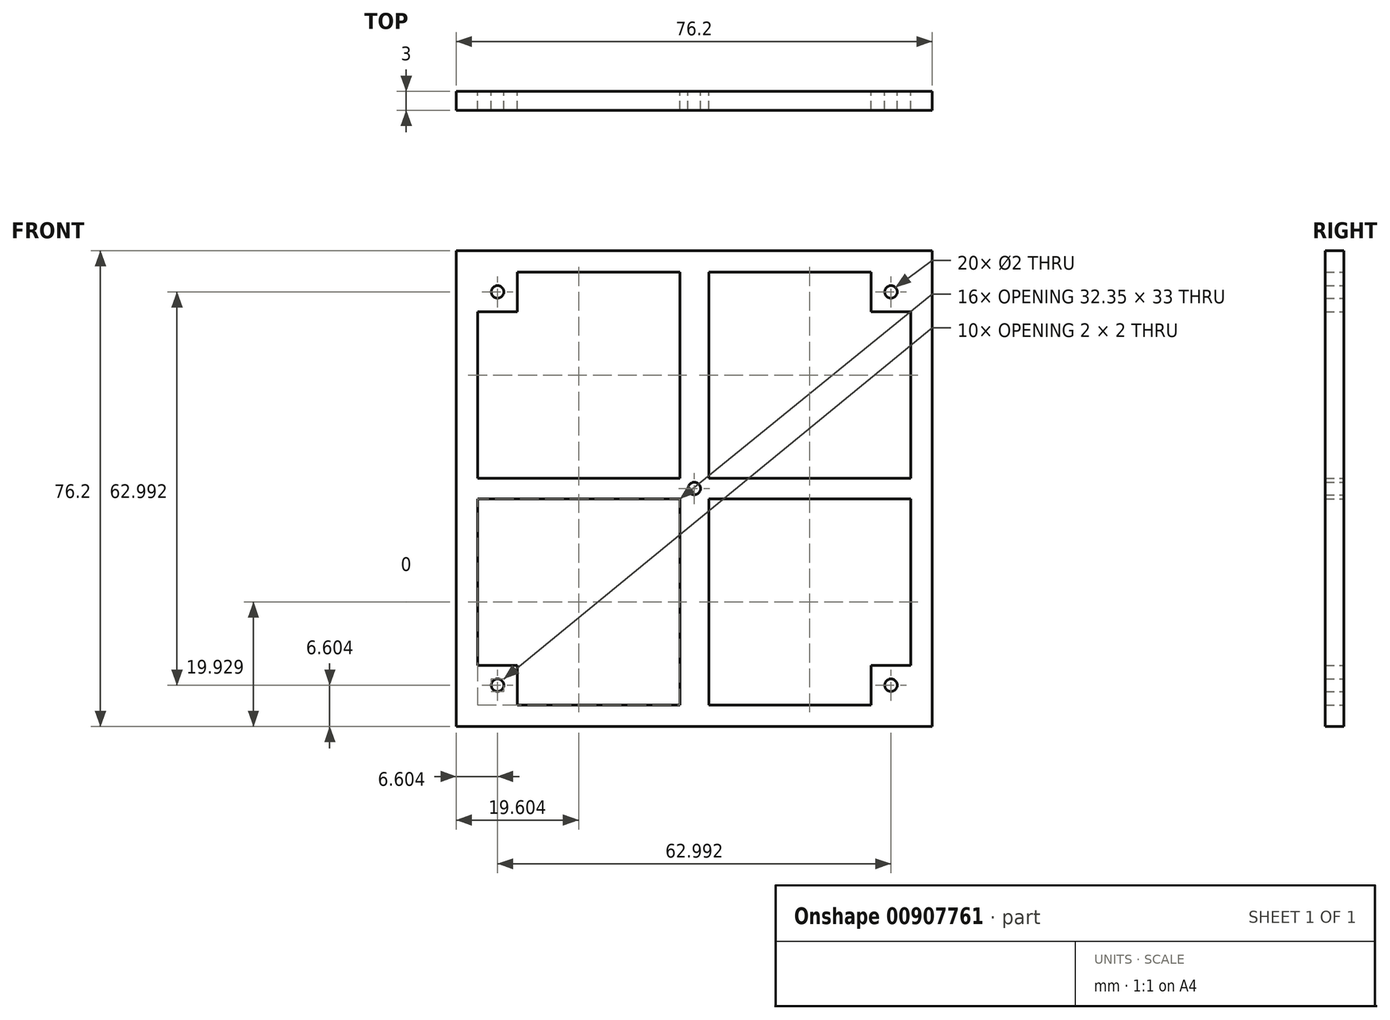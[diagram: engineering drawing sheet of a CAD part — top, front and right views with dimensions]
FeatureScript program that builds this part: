
annotation { "Feature Type Name" : "Feature", "Feature Type Description" : "" }
export const myFeature = defineFeature(function(context is Context, id is Id, definition is map)
    precondition{}
    {
        {
            var Q0;
            Q0=qCreatedBy(makeId("Front.planeOp"),FACE);
            var sketch = newSketch(context, id + "F0", { "sketchPlane" : qUnion([Q0])});
            skLineSegment(sketch, "E0.bottom", {"start": v(38.1, 38.1) * mm, "end": v(-38.1, 38.1) * mm});
            skLineSegment(sketch, "E0.top", {"start": v(38.1, -38.1) * mm, "end": v(-38.1, -38.1) * mm});
            skLineSegment(sketch, "E0.left", {"start": v(38.1, 38.1) * mm, "end": v(38.1, -38.1) * mm});
            skLineSegment(sketch, "E0.right", {"start": v(-38.1, 38.1) * mm, "end": v(-38.1, -38.1) * mm});
            skPoint(sketch, "E0.middle", {"position": v(0, 0) * mm});
            skPoint(sketch, "E1", {"position": v(-31.5, 31.5) * mm});
            skPoint(sketch, "E2", {"position": v(31.5, 31.5) * mm});
            skPoint(sketch, "E3", {"position": v(31.5, -31.5) * mm});
            skPoint(sketch, "E4", {"position": v(-31.5, -31.5) * mm});
            skLineSegment(sketch, "E5.bottom", {"start": v(-28.32, 34.67) * mm, "end": v(-34.67, 34.67) * mm});
            skLineSegment(sketch, "E5.top", {"start": v(-28.32, 28.32) * mm, "end": v(-34.67, 28.32) * mm});
            skLineSegment(sketch, "E5.left", {"start": v(-28.32, 34.67) * mm, "end": v(-28.32, 28.32) * mm});
            skLineSegment(sketch, "E5.right", {"start": v(-34.67, 34.67) * mm, "end": v(-34.67, 28.32) * mm});
            skLineSegment(sketch, "E6.bottom", {"start": v(34.67, 34.67) * mm, "end": v(28.32, 34.67) * mm});
            skLineSegment(sketch, "E6.top", {"start": v(34.67, 28.32) * mm, "end": v(28.32, 28.32) * mm});
            skLineSegment(sketch, "E6.left", {"start": v(34.67, 34.67) * mm, "end": v(34.67, 28.32) * mm});
            skLineSegment(sketch, "E6.right", {"start": v(28.32, 34.67) * mm, "end": v(28.32, 28.32) * mm});
            skLineSegment(sketch, "E7.bottom", {"start": v(34.67, -28.32) * mm, "end": v(28.32, -28.32) * mm});
            skLineSegment(sketch, "E7.top", {"start": v(34.67, -34.67) * mm, "end": v(28.32, -34.67) * mm});
            skLineSegment(sketch, "E7.left", {"start": v(34.67, -28.32) * mm, "end": v(34.67, -34.67) * mm});
            skLineSegment(sketch, "E7.right", {"start": v(28.32, -28.32) * mm, "end": v(28.32, -34.67) * mm});
            skLineSegment(sketch, "E8.bottom", {"start": v(-28.32, -28.32) * mm, "end": v(-34.67, -28.32) * mm});
            skLineSegment(sketch, "E8.top", {"start": v(-28.32, -34.67) * mm, "end": v(-34.67, -34.67) * mm});
            skLineSegment(sketch, "E8.left", {"start": v(-28.32, -28.32) * mm, "end": v(-28.32, -34.67) * mm});
            skLineSegment(sketch, "E8.right", {"start": v(-34.67, -28.32) * mm, "end": v(-34.67, -34.67) * mm});
            skLineSegment(sketch, "E9.bottom", {"start": v(-28.32, 34.67) * mm, "end": v(-2.32, 34.67) * mm});
            skLineSegment(sketch, "E9.top", {"start": v(-28.32, 1.67) * mm, "end": v(-2.32, 1.67) * mm});
            skLineSegment(sketch, "E9.left", {"start": v(-28.32, 34.67) * mm, "end": v(-28.32, 1.67) * mm});
            skLineSegment(sketch, "E9.right", {"start": v(-2.32, 34.67) * mm, "end": v(-2.32, 1.67) * mm});
            skLineSegment(sketch, "E10.bottom", {"start": v(28.32, 34.67) * mm, "end": v(2.32, 34.67) * mm});
            skLineSegment(sketch, "E10.top", {"start": v(28.32, 1.67) * mm, "end": v(2.32, 1.67) * mm});
            skLineSegment(sketch, "E10.left", {"start": v(28.32, 34.67) * mm, "end": v(28.32, 1.67) * mm});
            skLineSegment(sketch, "E10.right", {"start": v(2.32, 34.67) * mm, "end": v(2.32, 1.67) * mm});
            skLineSegment(sketch, "E11.bottom", {"start": v(-28.32, -34.67) * mm, "end": v(-2.32, -34.67) * mm});
            skLineSegment(sketch, "E11.top", {"start": v(-28.32, -1.67) * mm, "end": v(-2.32, -1.67) * mm});
            skLineSegment(sketch, "E11.left", {"start": v(-28.32, -34.67) * mm, "end": v(-28.32, -1.67) * mm});
            skLineSegment(sketch, "E11.right", {"start": v(-2.32, -34.67) * mm, "end": v(-2.32, -1.67) * mm});
            skLineSegment(sketch, "E12.bottom", {"start": v(28.32, -34.67) * mm, "end": v(2.32, -34.67) * mm});
            skLineSegment(sketch, "E12.top", {"start": v(28.32, -1.67) * mm, "end": v(2.32, -1.67) * mm});
            skLineSegment(sketch, "E12.left", {"start": v(28.32, -34.67) * mm, "end": v(28.32, -1.67) * mm});
            skLineSegment(sketch, "E12.right", {"start": v(2.32, -34.67) * mm, "end": v(2.32, -1.67) * mm});
            skLineSegment(sketch, "E13.top", {"start": v(34.67, 1.67) * mm, "end": v(28.32, 1.67) * mm});
            skLineSegment(sketch, "E13.left", {"start": v(34.67, 28.32) * mm, "end": v(34.67, 1.67) * mm});
            skLineSegment(sketch, "E13.right", {"start": v(28.32, 28.32) * mm, "end": v(28.32, 1.67) * mm});
            skLineSegment(sketch, "E14.bottom", {"start": v(28.32, -1.67) * mm, "end": v(34.67, -1.67) * mm});
            skLineSegment(sketch, "E14.top", {"start": v(28.32, -28.32) * mm, "end": v(34.67, -28.32) * mm});
            skLineSegment(sketch, "E14.left", {"start": v(28.32, -1.67) * mm, "end": v(28.32, -28.32) * mm});
            skLineSegment(sketch, "E14.right", {"start": v(34.67, -1.67) * mm, "end": v(34.67, -28.32) * mm});
            skLineSegment(sketch, "E15.top", {"start": v(-28.32, 1.67) * mm, "end": v(-34.67, 1.67) * mm});
            skLineSegment(sketch, "E15.left", {"start": v(-28.32, 28.32) * mm, "end": v(-28.32, 1.67) * mm});
            skLineSegment(sketch, "E15.right", {"start": v(-34.67, 28.32) * mm, "end": v(-34.67, 1.67) * mm});
            skLineSegment(sketch, "E16.bottom", {"start": v(-28.32, -1.67) * mm, "end": v(-34.67, -1.67) * mm});
            skLineSegment(sketch, "E16.left", {"start": v(-28.32, -1.67) * mm, "end": v(-28.32, -28.32) * mm});
            skLineSegment(sketch, "E16.right", {"start": v(-34.67, -1.67) * mm, "end": v(-34.67, -28.32) * mm});
            skSolve(sketch);
        }
        {
            var Q0;
            Q0=makeQuery(id+"F0.imprint","IMPRINT",FACE,{"disambiguationData":[TD([[makeQuery(id+"F0.imprint","IMPRINT",EDGE,{"derivedFrom":sQuery(id+"F0.wireOp",EDGE,"E0.bottom")}),1.0]])]});
            var Q1;
            Q1=makeQuery(id+"F0.imprint","IMPRINT",FACE,{"disambiguationData":[TD([[makeQuery(id+"F0.imprint","IMPRINT",EDGE,{"derivedFrom":sQuery(id+"F0.wireOp",EDGE,"E5.bottom")}),1.0]])]});
            var Q2;
            Q2=makeQuery(id+"F0.imprint","IMPRINT",FACE,{"disambiguationData":[TD([[makeQuery(id+"F0.imprint","IMPRINT",EDGE,{"derivedFrom":sQuery(id+"F0.wireOp",EDGE,"E6.bottom")}),1.0]])]});
            var Q3;
            Q3=makeQuery(id+"F0.imprint","IMPRINT",FACE,{"disambiguationData":[TD([[makeQuery(id+"F0.imprint","IMPRINT",EDGE,{"derivedFrom":sQuery(id+"F0.wireOp",EDGE,"E8.top")}),-1.0]])]});
            var Q4;
            Q4=makeQuery(id+"F0.imprint","IMPRINT",FACE,{"disambiguationData":[TD([[makeQuery(id+"F0.imprint","IMPRINT",EDGE,{"derivedFrom":sQuery(id+"F0.wireOp",EDGE,"E7.top")}),-1.0]])]});
            extrude(context, id + "F1", {"entities" : qUnion([Q0, Q1, Q2, Q3, Q4]), "depth" : 3 * mm, "offsetDistance" : 25 * mm});
        }
        {
            var Q0;
            Q0=sQuery(id+"F0.wireOp",VERTEX,"E1");
            var Q1;
            Q1=sQuery(id+"F0.wireOp",VERTEX,"E2");
            var Q2;
            Q2=sQuery(id+"F0.wireOp",VERTEX,"E0.middle");
            var Q3;
            Q3=sQuery(id+"F0.wireOp",VERTEX,"E4");
            var Q4;
            Q4=sQuery(id+"F0.wireOp",VERTEX,"E3");
            var Q5;
            Q5=makeQuery(id+"F1.opExtrude","SWEPT_BODY",BODY,{"disambiguationData":[OSD([sQuery(id+"F0.wireOp",EDGE,"E0.bottom"),sQuery(id+"F0.wireOp",EDGE,"E0.top"),sQuery(id+"F0.wireOp",EDGE,"E0.left"),sQuery(id+"F0.wireOp",EDGE,"E0.right"),sQuery(id+"F0.wireOp",EDGE,"E9.bottom"),sQuery(id+"F0.wireOp",EDGE,"E9.top"),sQuery(id+"F0.wireOp",EDGE,"E9.left"),sQuery(id+"F0.wireOp",EDGE,"E9.right"),sQuery(id+"F0.wireOp",EDGE,"E10.bottom"),sQuery(id+"F0.wireOp",EDGE,"E10.top"),sQuery(id+"F0.wireOp",EDGE,"E10.left"),sQuery(id+"F0.wireOp",EDGE,"E10.right"),sQuery(id+"F0.wireOp",EDGE,"E11.bottom"),sQuery(id+"F0.wireOp",EDGE,"E11.top"),sQuery(id+"F0.wireOp",EDGE,"E11.left"),sQuery(id+"F0.wireOp",EDGE,"E11.right"),sQuery(id+"F0.wireOp",EDGE,"E12.bottom"),sQuery(id+"F0.wireOp",EDGE,"E12.top"),sQuery(id+"F0.wireOp",EDGE,"E12.left"),sQuery(id+"F0.wireOp",EDGE,"E12.right"),sQuery(id+"F0.wireOp",EDGE,"E6.top"),sQuery(id+"F0.wireOp",EDGE,"E13.top"),sQuery(id+"F0.wireOp",EDGE,"E13.left"),sQuery(id+"F0.wireOp",EDGE,"E14.bottom"),sQuery(id+"F0.wireOp",EDGE,"E14.top"),sQuery(id+"F0.wireOp",EDGE,"E14.right"),sQuery(id+"F0.wireOp",EDGE,"E5.top"),sQuery(id+"F0.wireOp",EDGE,"E15.top"),sQuery(id+"F0.wireOp",EDGE,"E15.right"),sQuery(id+"F0.wireOp",EDGE,"E16.bottom"),sQuery(id+"F0.wireOp",EDGE,"E8.bottom"),sQuery(id+"F0.wireOp",EDGE,"E16.right")])]});
            hole(context, id + "F2", {"style" : HoleStyle.SIMPLE, "endStyle" : HoleEndStyle.THROUGH, "oppositeDirection" : true, "holeDiameter" : 2 * mm, "majorDiameter" : 5 * mm, "isTappedThrough" : true, "tappedDepth" : 12 * mm, "tapClearance" : 3, "locations" : qUnion([Q0, Q1, Q2, Q3, Q4]), "scope" : qUnion([Q5])});
        }
    });
